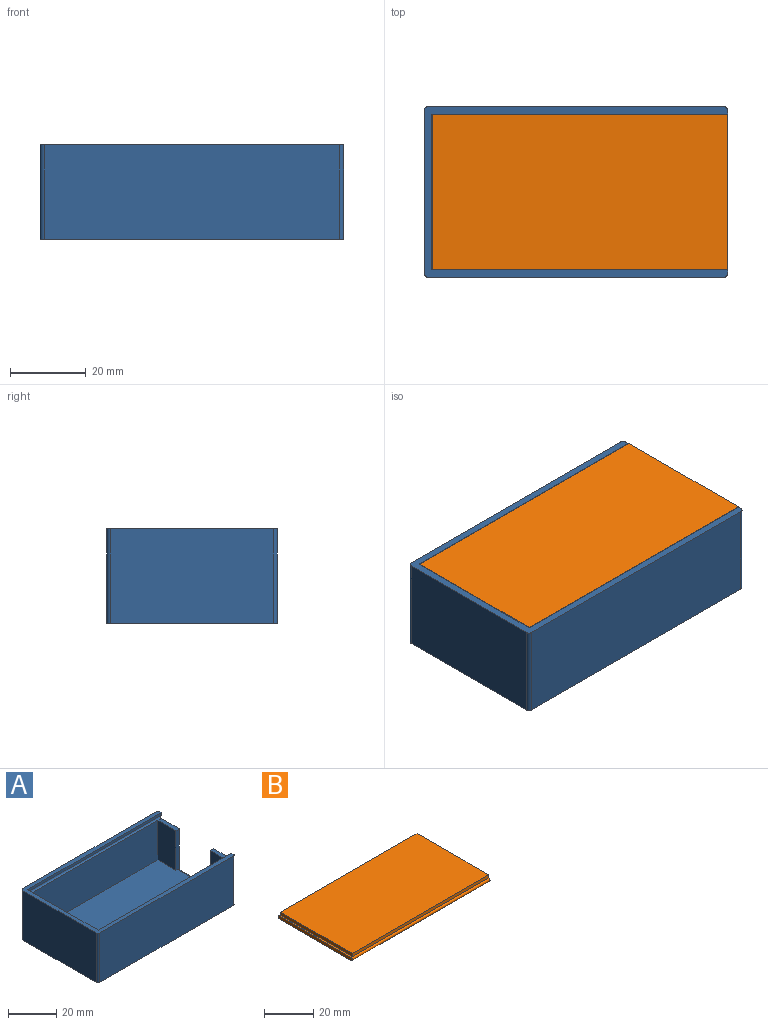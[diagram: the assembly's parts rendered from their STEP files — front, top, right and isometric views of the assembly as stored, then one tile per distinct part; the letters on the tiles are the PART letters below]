
ASSEMBLY  parts=2 mates=1
PART A: 29 faces, bbox 80x45x25 mm
  f0: plane 41x20mm, normal (1,0,0), area 820mm2, adj f10,f12,f14,f23
  f1: plane 78x1.3mm, normal (0,-1,0), area 101.4mm2, adj f3,f4,f11,f21
  f2: plane 78x1.3mm, normal (0,1,0), area 101.4mm2, adj f3,f4,f11,f19
  f3: plane 43x25mm, normal (1,0,0), area 529.7mm2, adj f1,f2,f4,f9,f15,f16,f17,f18
  f4: plane 80x45mm, normal (0,0,1), area 401.1mm2, adj f1,f2,f3,f6,f7,f8,f11,f25
  f5: plane 20x10.5mm, normal (-1,0,0), area 210mm2, adj f12,f14,f15,f16
  f6: plane 78x25mm, normal (0,1,0), area 1950mm2, adj f4,f9,f25,f28
  f7: plane 43x25mm, normal (-1,0,0), area 1075mm2, adj f4,f9,f25,f26
  f8: plane 78x25mm, normal (0,-1,0), area 1950mm2, adj f4,f9,f26,f27
  f9: plane 80x45mm, normal (0,0,-1), area 3599.1mm2, adj f3,f6,f7,f8,f25,f26,f27,f28
  f10: plane 76x20mm, normal (0,-1,0), area 1520mm2, adj f0,f13,f14,f21
  f11: plane 41x1.3mm, normal (1,0,0), area 53.3mm2, adj f1,f2,f4,f22
  f12: plane 76x20mm, normal (0,1,0), area 1520mm2, adj f0,f5,f14,f19
  f13: plane 20x10.5mm, normal (-1,0,0), area 210mm2, adj f10,f14,f17,f18
  f14: plane 77x41mm, normal (0,0,1), area 3136mm2, adj f0,f5,f10,f12,f13,f16,f17,f24
  f15: plane 10.5x2mm, normal (0,0,1), area 21mm2, adj f3,f5,f16,f19
  f16: plane 21x2mm, normal (0,1,0), area 40.2mm2, adj f3,f5,f14,f15,f24
  f17: plane 21x2mm, normal (0,-1,0), area 40.2mm2, adj f3,f13,f14,f18,f24
  f18: plane 10.5x2mm, normal (0,0,1), area 21mm2, adj f3,f13,f17,f21
  f19: cylinder r=0.85mm len=78.75mm, axis (1,0,0), area 210.3mm2, adj f2,f3,f12,f15,f20,f22,f23
  f20: plane 42.7x1.7mm, normal (1,0,0), area 72mm2, adj f19,f21,f22,f23
  f21: cylinder r=0.85mm len=78.75mm, axis (1,0,0), area 210.3mm2, adj f1,f3,f10,f18,f20,f22,f23
  f22: plane 41x0.75mm, normal (0,0,-1), area 30.8mm2, adj f11,f19,f20,f21
  f23: plane 41x0.75mm, normal (0,0,1), area 30.8mm2, adj f0,f19,f20,f21
  f24: cylinder r=1mm len=20mm, axis (0,1,0), area 31.4mm2, adj f3,f14,f16,f17
  f25: cylinder r=1mm len=25mm, axis (0,0,1), area 39.3mm2, adj f4,f6,f7,f9
  f26: cylinder r=1mm len=25mm, axis (0,0,-1), area 39.3mm2, adj f4,f7,f8,f9
  f27: cylinder r=1mm len=25mm, axis (0,0,1), area 39.3mm2, adj f3,f4,f8,f9
  f28: cylinder r=1mm len=25mm, axis (0,0,-1), area 39.3mm2, adj f3,f4,f6,f9
PART B: 14 faces, bbox 78.8x42.5x13 mm
  f0: plane 42.5x1.5mm, normal (-1,0,0), area 63.3mm2, adj f2,f3,f4,f8
  f1: plane 78x1.5mm, normal (0,-1,0), area 117mm2, adj f2,f6,f7,f9
  f2: cylinder r=0.75mm len=78.75mm, axis (-1,0,0), area 185.6mm2, adj f0,f1,f3,f7,f8
  f3: plane 78.75x41mm, normal (0,0,-1), area 3188.8mm2, adj f0,f2,f4,f7,f10,f11,f12
  f4: cylinder r=0.75mm len=78.75mm, axis (-1,0,0), area 185.6mm2, adj f0,f3,f5,f7,f8
  f5: plane 78x1.5mm, normal (0,1,0), area 117mm2, adj f4,f6,f7,f9
  f6: plane 78x41mm, normal (0,0,1), area 3198mm2, adj f1,f5,f7,f9
  f7: plane 42.5x12mm, normal (1,0,0), area 304.8mm2, adj f1,f2,f3,f4,f5,f6,f10,f12
  f8: plane 41x0.75mm, normal (0,0,1), area 30.8mm2, adj f0,f2,f4,f9
  f9: plane 41x1.5mm, normal (-1,0,0), area 61.5mm2, adj f1,f5,f6,f8
  f10: plane 10x2mm, normal (0,-1,0), area 19.6mm2, adj f3,f7,f11,f13
  f11: plane 20x9mm, normal (-1,0,0), area 180mm2, adj f3,f10,f12,f13
  f12: plane 10x2mm, normal (0,1,0), area 19.6mm2, adj f3,f7,f11,f13
  f13: cylinder r=1mm len=20mm, axis (0,1,0), area 62.8mm2, adj f7,f10,f11,f12
PLACE A rot(axis=(0.25,-0.09,0.96),0deg) t=(3.82,-4.76,-0.51)mm
PLACE B rot(axis=(0.25,-0.09,0.96),0deg) t=(4.5,-4.76,10.59)mm
MATE slider B.f2 <-> A.f19  axis (-1,0,0) through (4.5,-25.26,9.84)mm
